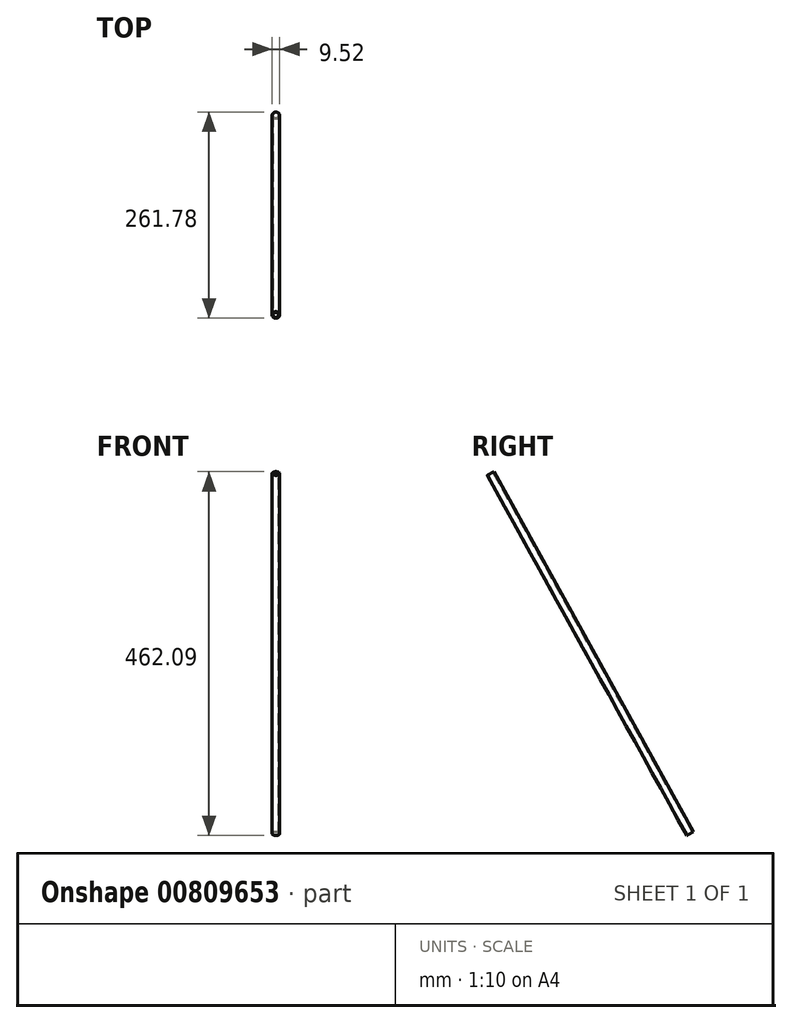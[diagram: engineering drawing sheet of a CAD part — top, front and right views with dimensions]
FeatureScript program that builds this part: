
annotation { "Feature Type Name" : "Feature", "Feature Type Description" : "" }
export const myFeature = defineFeature(function(context is Context, id is Id, definition is map)
    precondition{}
    {
        {
            var Q0;
            Q0=qCreatedBy(makeId("Front.planeOp"),FACE);
            cPlane(context, id + "F0", {"entities" : qUnion([Q0]), "cplaneType" : CPlaneType.OFFSET, "offset" : 127 * mm, "width" : 152.4 * mm, "height" : 152.4 * mm});
        }
        {
            var Q0;
            Q0=qCreatedBy(id+"F0.planeOp",FACE);
            var sketch = newSketch(context, id + "F1", { "sketchPlane" : qUnion([Q0])});
            skPoint(sketch, "E0", {"position": v(0, 0) * mm});
            skPoint(sketch, "E1", {"position": v(127, 0) * mm});
            skSolve(sketch);
        }
        {
            var Q0;
            Q0=qCreatedBy(makeId("Front.planeOp"),FACE);
            var sketch = newSketch(context, id + "F2", { "sketchPlane" : qUnion([Q0])});
            skPoint(sketch, "E2", {"position": v(0, 70.36) * mm});
            skSolve(sketch);
        }
        {
            var Q0;
            Q0=sQuery(id+"F2.wireOp",VERTEX,"E2");
            var Q1;
            Q1=sQuery(id+"F1.wireOp",VERTEX,"E1");
            var Q2;
            Q2=sQuery(id+"F1.wireOp",VERTEX,"E0");
            cPlane(context, id + "F3", {"entities" : qUnion([Q0, Q1, Q2]), "cplaneType" : CPlaneType.THREE_POINT, "offset" : 25.4 * mm, "width" : 152.4 * mm, "height" : 152.4 * mm});
        }
        {
            var Q0;
            Q0=qCreatedBy(id+"F3.planeOp",FACE);
            var sketch = newSketch(context, id + "F4", { "sketchPlane" : qUnion([Q0])});
            skCircle(sketch, "E3", {"center": v(0, -111.1) * mm, "radius": 3.52 * mm});
            skCircle(sketch, "E4", {"center": v(0, -111.1) * mm, "radius": 4.76 * mm});
            skSolve(sketch);
        }
        {
            var Q0;
            Q0=makeQuery(id+"F4.imprint","IMPRINT",FACE,{"disambiguationData":[TD([[makeQuery(id+"F4.imprint","IMPRINT",EDGE,{"derivedFrom":sQuery(id+"F4.wireOp",EDGE,"E3")}),-1.0]])]});
            extrude(context, id + "F5", {"entities" : qUnion([Q0]), "oppositeDirection" : true, "depth" : 523 * mm, "offsetDistance" : 25.4 * mm});
        }
    });
